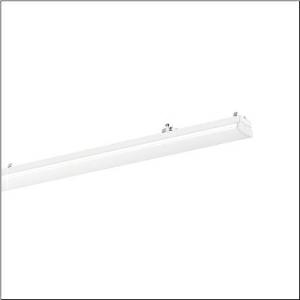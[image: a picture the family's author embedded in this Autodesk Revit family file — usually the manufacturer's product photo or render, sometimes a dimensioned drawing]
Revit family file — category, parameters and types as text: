
# Revit family: licross_r__21_recessed_opal_mo_52tl1d7n48xg_bf27
name_source: partatom
category: Lighting Fixtures
units: mm (PartAtom-declared; Revit-internal decimal feet)

## family parameters
Cut with Voids When Loaded = No
Host = Face
Light Source = No
Part Type = Normal
Room Calculation Point = No
Round Connector Dimension = Use Diameter
Shared = No

## types (1)
- Licross® 21 recessed opal MO (1 x LED, 8360 lm, 47.9 W, 4000K)
    Apparent Load = 48 VA
    CIE Flux Codes = 44 73 91 87 100
    Color Rendering = 80
    Color Temperature = 4000K
    Default Elevation = 1800 mm
    Description = Licross® 21 recessed opal MO, luminaire insert, of sheet steel, galvanised, coil coated, white, length: 1.500mm, width: 66mm, height: 67mm, LED rated luminous flux: 8.360lm, light colour: 840, control gear: ON/OFF, with plug, 3-pole, with phase selection, mains connection: 220..240V, AC, 50/60Hz, rated input power: 48W, internal wiring halogen-free, primary optical cover: cover, of PMMA, light emission: direct with ceiling illumination distribution, primary light characteristic: symmetric, protection rating (complete): IP40, insulation class (complete): insulation class I (protective earthing), certification: CE, ENEC, VDE, UKCA, protection symbol: D if used in an environment without relevant dust loads with corresponding accessories, impact resistance: IK06, permissible ambient temperature for indoor applications: -35..+40°C, corresponds to IFS (International Featured Standards) requirements for safety and quality in the food industry, reducing of maximum allowable ambient temperature of 5°C with ceiling mounting, LABS conformity tested according to VDMA 24364:2018-05, packaging unit: 1 piece
    Height = 83 mm
    Lamp = 1 x LED
    Lamp Light Flux = 8360 lm
    Lamp Power = 47.9 W
    Lamp count = 1
    Length = 1500 mm
    Luminous efficacy = 175 lm/W
    Manufacturer = Siteco
    ModVariant = No
    Model = 52TL1D7N48XG
    Mounting Place = Ceiling
    Mounting Type = Pendant
    Number of Poles = 1
    OnlyDefault = Yes
    Power Factor = 1
    Product Name = Licross® 21 recessed opal MO
    Product group = luminaire insert | ceiling pendant
    ProductGroupID = 902
    Protection Class = Protection class I
    Protection Degree = IP 40
    RLX_Detail_Level = 1
    RLX_Emergency_Light_Flux = 0 lm
    RLX_Emergency_Type = 0
    RLX_Emergency_Type_DB = No
    RlxData = <blob elided: 23077 chars, md5=a44adfcc>
    Socket = socket
    Standby Power = 0 W
    System Light Flux = 8360 lm
    System Power = 48 W
    Type Comments = Product without accessories
    Type Image = l_1313666.jpg
    URL = http://relux.com
    VarID = ---
    Voltage = 0 V
    Weight = 0.00 kg
    Width = 76 mm

## geometry (parser evidence)
native form markers: Blend x4, Sweep x14
no freeform markers — native parametric forms only
